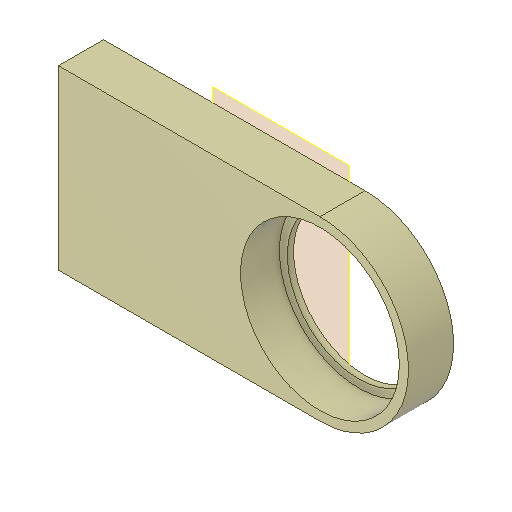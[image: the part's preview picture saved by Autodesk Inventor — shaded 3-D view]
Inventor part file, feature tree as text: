
AUTODESK INVENTOR PART (.ipt)
format: ipt  version: 2022 (Build 260153000, 153)  size: 134,656 bytes
history: native  units: mm
features: extrude x2, sketch x2, reference x2, other x2, plane x1, projected_geometry x1
ambient origin geometry x8: Origin, YZ Plane, XZ Plane, XY Plane, X Axis, Y Axis, Z Axis, Center Point
bodies: Solid1 (feature_tree)
feature tree (10):
  plane  "Work Plane1"
  extrude  "Extrusion1"  Depth=25.55mm
  extrude  "Extrusion2"  Depth=1.0mm TaperAngle=0.0deg
  sketch  "Sketch1"  dims[d0=0.75mm d1=25.55mm]
  reference  "Reference1"
  reference  "Reference2"
  sketch  "Sketch2"  dims[d2=23.0mm d3=1.0mm d4=0.0mm d5=25.55mm d6=6.25mm d7=0.0mm]
  projected_geometry  "Projected Loop1"
  other  "Assembly_Axiotech_Eypiece.iam"
  other  "00_Fluegeladapter:1"
